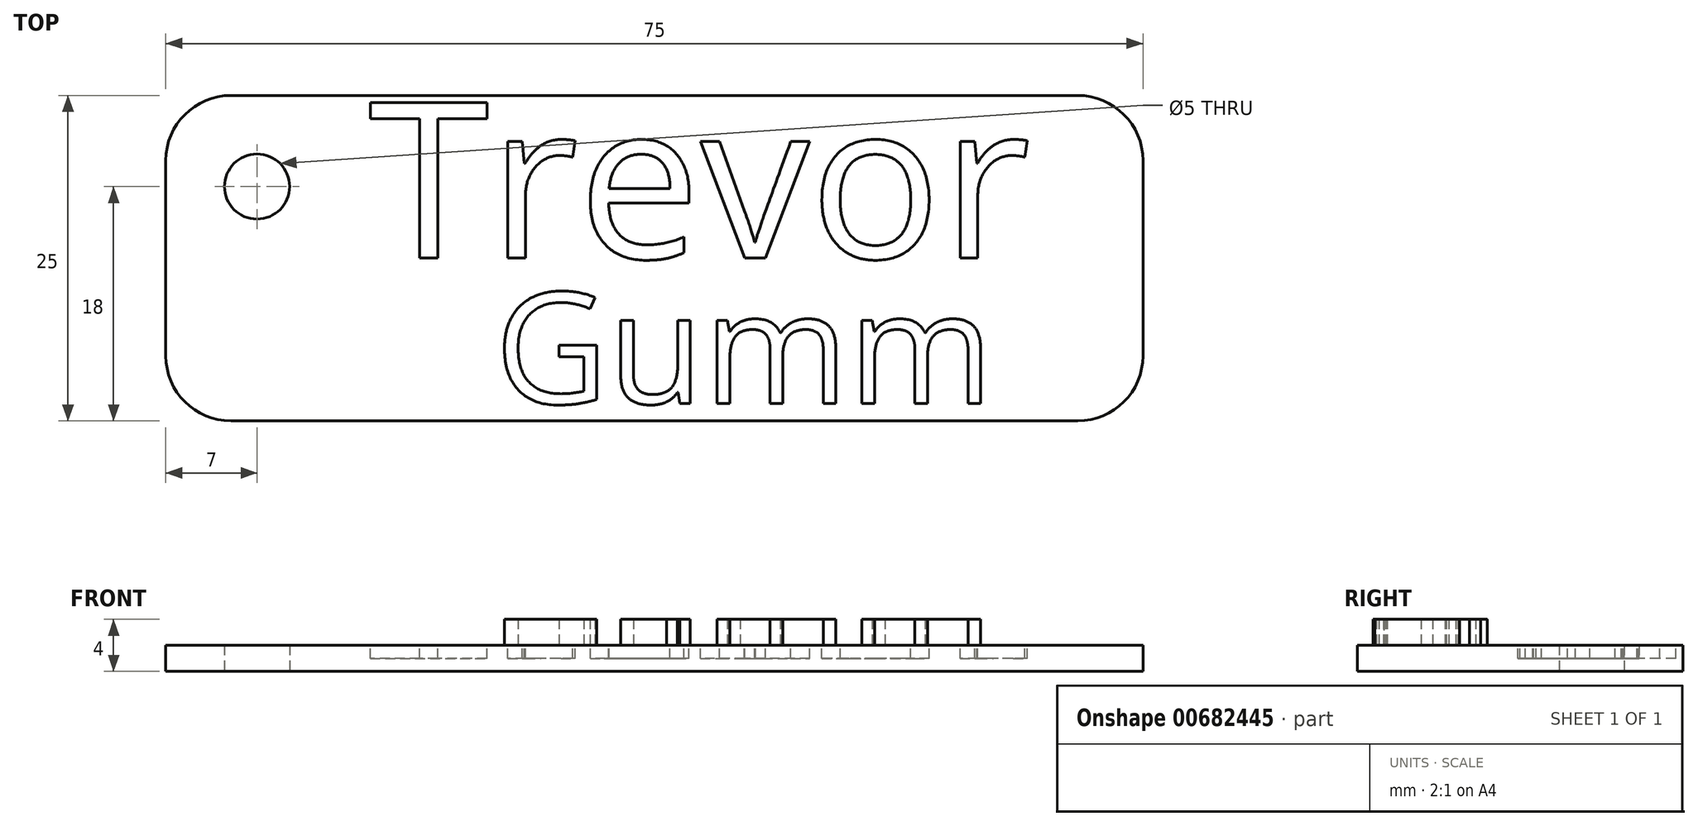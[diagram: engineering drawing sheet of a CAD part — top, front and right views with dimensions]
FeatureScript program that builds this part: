
annotation { "Feature Type Name" : "Feature", "Feature Type Description" : "" }
export const myFeature = defineFeature(function(context is Context, id is Id, definition is map)
    precondition{}
    {
        {
            var Q0;
            Q0=qCreatedBy(makeId("Top.planeOp"),FACE);
            var sketch = newSketch(context, id + "F0", { "sketchPlane" : qUnion([Q0])});
            skLineSegment(sketch, "E0.bottom", {"start": v(32.5, -12.5) * mm, "end": v(-32.5, -12.5) * mm});
            skLineSegment(sketch, "E0.top", {"start": v(32.5, 12.5) * mm, "end": v(-32.5, 12.5) * mm});
            skLineSegment(sketch, "E0.left", {"start": v(37.5, -7.5) * mm, "end": v(37.5, 7.5) * mm});
            skLineSegment(sketch, "E0.right", {"start": v(-37.5, -7.5) * mm, "end": v(-37.5, 7.5) * mm});
            skPoint(sketch, "E0.middle", {"position": v(0, 0) * mm});
            skPoint(sketch, "E1.visualSharp", {"position": v(-37.5, 12.5) * mm});
            skArc(sketch, "E1.filletArc", {"start": v(-32.5, 12.5) * mm, "mid": v(-36.04, 11.04) * mm, "end": v(-37.5, 7.5) * mm});
            skPoint(sketch, "E2.visualSharp", {"position": v(-37.5, -12.5) * mm});
            skArc(sketch, "E2.filletArc", {"start": v(-37.5, -7.5) * mm, "mid": v(-36.04, -11.04) * mm, "end": v(-32.5, -12.5) * mm});
            skPoint(sketch, "E3.visualSharp", {"position": v(37.5, -12.5) * mm});
            skArc(sketch, "E3.filletArc", {"start": v(32.5, -12.5) * mm, "mid": v(36.04, -11.04) * mm, "end": v(37.5, -7.5) * mm});
            skPoint(sketch, "E4.visualSharp", {"position": v(37.5, 12.5) * mm});
            skArc(sketch, "E4.filletArc", {"start": v(37.5, 7.5) * mm, "mid": v(36.04, 11.04) * mm, "end": v(32.5, 12.5) * mm});
            skSolve(sketch);
        }
        {
            var Q0;
            Q0 = qSketchRegion(id + "F0", true);
            extrude(context, id + "F1", {"entities" : qUnion([Q0]), "depth" : 2 * mm, "offsetDistance" : 25 * mm});
        }
        {
            var Q0;
            Q0=qCreatedBy(makeId("Top.planeOp"),FACE);
            var sketch = newSketch(context, id + "F2", { "sketchPlane" : qUnion([Q0])});
            skPoint(sketch, "E5", {"position": v(-30.5, 5.5) * mm});
            skSolve(sketch);
        }
        {
            var Q0;
            Q0=sQuery(id+"F2.wireOp",VERTEX,"E5");
            var Q1;
            Q1=makeQuery(id+"F1.opExtrude","SWEPT_BODY",BODY,{"disambiguationData":[OSD([sQuery(id+"F0.wireOp",EDGE,"E0.bottom"),sQuery(id+"F0.wireOp",EDGE,"E0.top"),sQuery(id+"F0.wireOp",EDGE,"E0.left"),sQuery(id+"F0.wireOp",EDGE,"E0.right"),sQuery(id+"F0.wireOp",EDGE,"E1.filletArc"),sQuery(id+"F0.wireOp",EDGE,"E2.filletArc"),sQuery(id+"F0.wireOp",EDGE,"E3.filletArc"),sQuery(id+"F0.wireOp",EDGE,"E4.filletArc")])]});
            hole(context, id + "F3", {"style" : HoleStyle.SIMPLE, "endStyle" : HoleEndStyle.THROUGH, "oppositeDirection" : true, "holeDiameter" : 5 * mm, "majorDiameter" : 5 * mm, "isTappedThrough" : true, "tappedDepth" : 12 * mm, "tapClearance" : 3, "locations" : qUnion([Q0]), "scope" : qUnion([Q1])});
        }
        {
            var Q0;
            Q0=makeQuery(id+"F1.opExtrude","CAP_FACE",FACE,{"disambiguationData":[OSD([sQuery(id+"F0.wireOp",EDGE,"E0.bottom"),sQuery(id+"F0.wireOp",EDGE,"E0.top"),sQuery(id+"F0.wireOp",EDGE,"E0.left"),sQuery(id+"F0.wireOp",EDGE,"E0.right"),sQuery(id+"F0.wireOp",EDGE,"E1.filletArc"),sQuery(id+"F0.wireOp",EDGE,"E2.filletArc"),sQuery(id+"F0.wireOp",EDGE,"E3.filletArc"),sQuery(id+"F0.wireOp",EDGE,"E4.filletArc")])],"isStart":false});
            var sketch = newSketch(context, id + "F4", { "sketchPlane" : qUnion([Q0])});
            skText(sketch, "E6", { "text": "Trevor", "fontName": "OpenSans-Regular.ttf"});
            const initialGuessF4  = {"E6": [-0.02195, 0, 1, 0, 0.01205]};
            skSetInitialGuess(sketch, initialGuessF4);
            skSolve(sketch);
        }
        {
            var Q0;
            Q0 = qSketchRegion(id + "F4", true);
            extrude(context, id + "F5", {"entities" : qUnion([Q0]), "operationType" : NewBodyOperationType.REMOVE, "oppositeDirection" : true, "depth" : 1 * mm, "offsetDistance" : 25 * mm});
        }
        {
            var Q0;
            {var subQ0=sQuery(id+"F0.wireOp",EDGE,"E1.filletArc");var subQ1=sQuery(id+"F0.wireOp",EDGE,"E0.top");var subQ2=sQuery(id+"F0.wireOp",EDGE,"E4.filletArc");var subQ3=sQuery(id+"F0.wireOp",EDGE,"E3.filletArc");var subQ4=sQuery(id+"F0.wireOp",EDGE,"E2.filletArc");var subQ5=sQuery(id+"F0.wireOp",EDGE,"E0.bottom");var subQ6=sQuery(id+"F0.wireOp",EDGE,"E0.left");var subQ7=sQuery(id+"F0.wireOp",EDGE,"E0.right");Q0=makeQuery(id+"F5.boolean.opBoolean","SPLIT",FACE,{"disambiguationData":[TD([makeQuery(id+"F1.opExtrude","SWEPT_FACE",FACE,{"disambiguationData":[OSD([subQ5])]})])],"derivedFrom":makeQuery(id+"F1.opExtrude","CAP_FACE",FACE,{"disambiguationData":[OSD([subQ5,subQ1,subQ6,subQ7,subQ0,subQ4,subQ3,subQ2])],"isStart":false})});}
            var sketch = newSketch(context, id + "F6", { "sketchPlane" : qUnion([Q0])});
            skText(sketch, "E7", { "text": "Gumm\n", "fontName": "OpenSans-Regular.ttf"});
            const initialGuessF6  = {"E7": [-0.01224, -0.01117, 1, 0, 0.0086]};
            skSetInitialGuess(sketch, initialGuessF6);
            skSolve(sketch);
        }
        {
            var Q0;
            Q0 = qSketchRegion(id + "F6", true);
            extrude(context, id + "F7", {"entities" : qUnion([Q0]), "operationType" : NewBodyOperationType.ADD, "depth" : 2 * mm, "offsetDistance" : 25 * mm});
        }
    });
